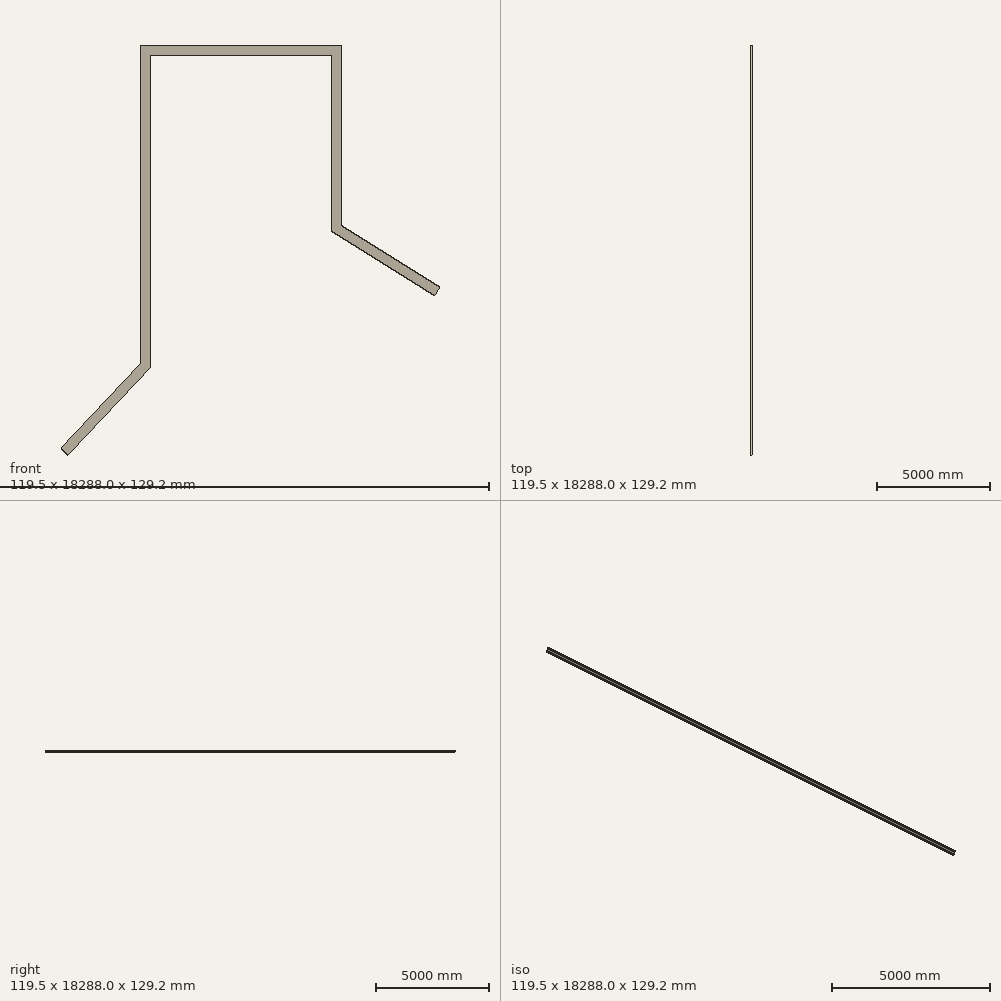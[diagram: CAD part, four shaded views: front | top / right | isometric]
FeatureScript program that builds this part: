
annotation { "Feature Type Name" : "Feature", "Feature Type Description" : "" }
export const myFeature = defineFeature(function(context is Context, id is Id, definition is map)
    precondition{}
    {
        {
            var Q0;
            Q0=qCreatedBy(makeId("Front.planeOp"),FACE);
            var sketch = newSketch(context, id + "F0", { "sketchPlane" : qUnion([Q0])});
            skLineSegment(sketch, "E0", {"start": v(0, 0) * mm, "end": v(25.04, 26.6) * mm});
            skLineSegment(sketch, "E1", {"start": v(25.04, 26.6) * mm, "end": v(25.04, 127) * mm});
            skLineSegment(sketch, "E2", {"start": v(25.04, 127) * mm, "end": v(88.54, 127) * mm});
            skLineSegment(sketch, "E3", {"start": v(88.54, 127) * mm, "end": v(88.54, 70.17) * mm});
            skLineSegment(sketch, "E4", {"start": v(88.54, 70.17) * mm, "end": v(119.52, 50.8) * mm});
            skLineSegment(sketch, "E5.0", {"start": v(2.31, -2.18) * mm, "end": v(28.22, 25.34) * mm});
            skLineSegment(sketch, "E6.0", {"start": v(28.22, 25.34) * mm, "end": v(28.22, 123.83) * mm});
            skLineSegment(sketch, "E7.0", {"start": v(28.22, 123.83) * mm, "end": v(85.37, 123.83) * mm});
            skLineSegment(sketch, "E8.0", {"start": v(85.37, 123.83) * mm, "end": v(85.37, 68.4) * mm});
            skLineSegment(sketch, "E9.0", {"start": v(85.37, 68.4) * mm, "end": v(117.84, 48.1) * mm});
            skLineSegment(sketch, "E10", {"start": v(0, 0) * mm, "end": v(2.31, -2.18) * mm});
            skLineSegment(sketch, "E11", {"start": v(117.84, 48.1) * mm, "end": v(119.52, 50.8) * mm});
            skSolve(sketch);
        }
        {
            var Q0;
            Q0=makeQuery(id+"F0.imprint","IMPRINT",FACE,{"disambiguationData":[TD([[makeQuery(id+"F0.imprint","IMPRINT",EDGE,{"derivedFrom":sQuery(id+"F0.wireOp",EDGE,"E0")}),-1.0]])]});
            extrude(context, id + "F1", {"entities" : qUnion([Q0]), "oppositeDirection" : true, "depth" : 18288 * mm, "offsetDistance" : 25.4 * mm});
        }
    });
